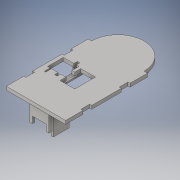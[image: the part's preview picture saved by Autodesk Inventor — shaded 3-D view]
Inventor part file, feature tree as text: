
AUTODESK INVENTOR PART (.ipt)
format: ipt  version: 2016 (Build 200138000, 138)  size: 532,480 bytes
history: native  units: in
note: dims shown in document units (in); Inventor stores cm internally (conversion verified against a paired STEP export)
features: reference x54, extrude x26, sketch x25, plane x6, projected_geometry x2
ambient origin geometry x8: Origin, YZ Plane, XZ Plane, XY Plane, X Axis, Y Axis, Z Axis, Center Point
bodies: Solid1 (feature_tree)
feature tree (113):
  extrude  "Extrusion1"  Depth=3.0in
  extrude  "Extrusion2"  Depth=0.0787in
  extrude  "Extrusion3"  Depth=1.0in
  extrude  "Extrusion4"  Depth=1.0in TaperAngle=0.0deg
  extrude  "Extrusion5"  Depth=0.0197in
  plane  "Work Plane1"
  extrude  "Extrusion6"  Depth=0.0197in
  extrude  "Extrusion7"  Depth=0.0197in
  extrude  "Extrusion8"  Depth=0.0787in
  extrude  "Extrusion9"  Depth=0.303in TaperAngle=0.0deg
  extrude  "Extrusion14"  Depth=0.1575in
  extrude  "Extrusion15"  Depth=0.0787in
  plane  "Work Plane2"
  extrude  "Extrusion16"  Depth=0.1181in TaperAngle=0.0deg
  extrude  "Extrusion17"  Depth=0.1575in
  extrude  "Extrusion18"  Depth=0.1181in TaperAngle=0.0deg
  extrude  "Extrusion19"  Depth=0.0197in
  plane  "Work Plane3"
  extrude  "Extrusion20"  Depth=0.0197in
  extrude  "Extrusion21"  Depth=0.0787in
  plane  "Work Plane4"
  extrude  "Extrusion22"  Depth=1.5748in TaperAngle=0.0deg
  plane  "Work Plane5"
  extrude  "Extrusion23"  Depth=0.9201in TaperAngle=0.0deg
  extrude  "Extrusion24"  Depth=0.1969in
  plane  "Work Plane6"
  extrude  "Extrusion25"  Depth=0.1969in TaperAngle=0.0deg
  extrude  "Extrusion26"  Depth=0.1181in TaperAngle=0.0deg
  extrude  "Extrusion27"  Depth=0.1181in
  extrude  "Extrusion28"  Depth=0.1969in TaperAngle=0.0deg
  extrude  "Extrusion29"  Depth=0.0394in
  extrude  "Extrusion30"  Depth=0.35in
  sketch  "Sketch1"  dims[d0=4.5in d1=3.0in]
  sketch  "Sketch2"  dims[d2=0.1969in d3=0.0in d5=0.0787in]
  reference  "Reference1"
  reference  "Reference2"
  sketch  "Sketch3"  dims[d6=1.0in d7=0.0in d8=1.0827in]
  sketch  "Sketch4"  dims[d9=0.3937in d10=1.0in d11=0.0in]
  reference  "Reference3"
  reference  "Reference4"
  reference  "Reference5"
  reference  "Reference6"
  reference  "Reference7"
  reference  "Reference8"
  reference  "Reference9"
  reference  "Reference10"
  reference  "Reference11"
  reference  "Reference12"
  reference  "Reference13"
  sketch  "Sketch5"  dims[d12=0.0787in d13=0.0197in]
  reference  "Reference14"
  reference  "Reference15"
  reference  "Reference16"
  reference  "Reference17"
  reference  "Reference18"
  sketch  "Sketch6"  dims[d14=0.0197in d15=0.0197in]
  reference  "Reference19"
  sketch  "Sketch7"  dims[d16=0.0197in d17=0.0197in]
  reference  "Reference20"
  reference  "Reference21"
  reference  "Reference22"
  reference  "Reference23"
  reference  "Reference24"
  sketch  "Sketch8"  dims[d18=0.0787in d19=0.0787in]
  reference  "Reference25"
  sketch  "Sketch9"  dims[d20=0.0787in d21=0.303in d22=0.0in]
  projected_geometry  "Projected Loop1"
  projected_geometry  "Projected Loop2"
  sketch  "Sketch14"  dims[d23=0.0098in d24=0.1575in]
  sketch  "Sketch15"  dims[d25=0.0787in d26=0.0098in]
  sketch  "Sketch16"  dims[d27=0.1575in d28=0.1181in d29=0.0in]
  reference  "Reference30"
  sketch  "Sketch17"  dims[d30=1.25in d31=0.1575in]
  reference  "Reference31"
  reference  "Reference32"
  reference  "Reference33"
  reference  "Reference35"
  reference  "Reference36"
  reference  "Reference37"
  reference  "Reference38"
  reference  "Reference39"
  reference  "Reference40"
  reference  "Reference41"
  reference  "Reference42"
  reference  "Reference43"
  reference  "Reference44"
  reference  "Reference45"
  reference  "Reference46"
  reference  "Reference47"
  reference  "Reference48"
  reference  "Reference49"
  sketch  "Sketch19"  dims[d32=0.1575in d33=0.1181in d34=0.0in]
  sketch  "Sketch20"  dims[d35=0.0197in d36=0.0197in]
  reference  "Reference50"
  sketch  "Sketch21"  dims[d37=0.0197in d38=0.0197in]
  sketch  "Sketch22"  dims[d39=0.0787in d40=0.0787in]
  reference  "Reference51"
  reference  "Reference52"
  sketch  "Sketch23"  dims[d41=0.0787in d42=1.5748in d43=0.0in]
  reference  "Reference53"
  reference  "Reference54"
  sketch  "Sketch24"  dims[d44=0.1801in d45=0.0in d46=0.9201in d47=0.0in]
  sketch  "Sketch25"  dims[d58=0.1969in d59=0.1969in]
  reference  "Reference55"
  reference  "Reference56"
  sketch  "Sketch26"  dims[d60=0.1969in d61=0.1969in d62=0.0in]
  reference  "Reference57"
  reference  "Reference58"
  sketch  "Sketch28"  dims[d63=1.0in d64=0.0in d65=0.1181in d66=0.0in]
  sketch  "Sketch29"  dims[d67=0.1969in d68=0.0in d69=0.1181in]
  sketch  "Sketch30"  dims[d70=0.1181in d71=0.1969in d72=0.0in]
  reference  "Reference59"
  sketch  "Sketch31"  dims[d73=0.0787in d74=0.0in d75=0.0394in d76=0.35in d77=0.1628in d78=0.2in d79=0.0787in d80=0.0in d81=0.1969in d82=0.0in d83=0.0098in d84=0.0787in d85=0.0098in d86=0.0787in d87=0.315in d88=0.0in d89=1.5in d90=1.5in d91=0.1181in d92=0.0in d93=0.7in d94=1.26in d95=0.0in d96=0.1181in d97=0.0in d98=0.1181in d99=0.0in d104=1.0in d105=0.1181in d106=0.5in d107=1.0in d108=0.5in d109=10.0in d110=0.0in d111=0.0197in d112=0.0197in d113=0.325in d114=0.197in d115=0.0in d116=0.1969in d117=0.1969in d118=0.1181in d119=0.1969in d120=0.0in d121=0.1575in d122=0.0in]
